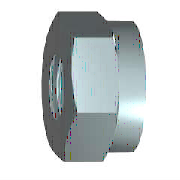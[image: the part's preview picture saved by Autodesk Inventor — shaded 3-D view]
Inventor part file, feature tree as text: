
AUTODESK INVENTOR PART (.ipt)
format: ipt  version: 2024 (Build 280153000, 153)  size: 178,688 bytes
history: native  units: mm (DEFAULTED — no unit token found)
features: extrude x2, other x2, hole x1, plane x1
ambient origin geometry x7: Origin, YZ Plane, XZ Plane, X Axis, Y Axis, Z Axis, Center Point
bodies: Solid1 (feature_tree)
feature tree (6):
  extrude  "Базовый элемент"  Depth=8.082904mm
  extrude  "Кольцо"  Depth=2.9mm
  other  "Фаска1"
  hole  "Резьба"  [1 undecoded]
  other  "Work Axis1"
  plane  "Work Plane1"
note: 1 required parameter value undecoded (feature->parameter linkage not recoverable at this tier; creation-order binding heuristic only, values carry confidence <= 0.55)
